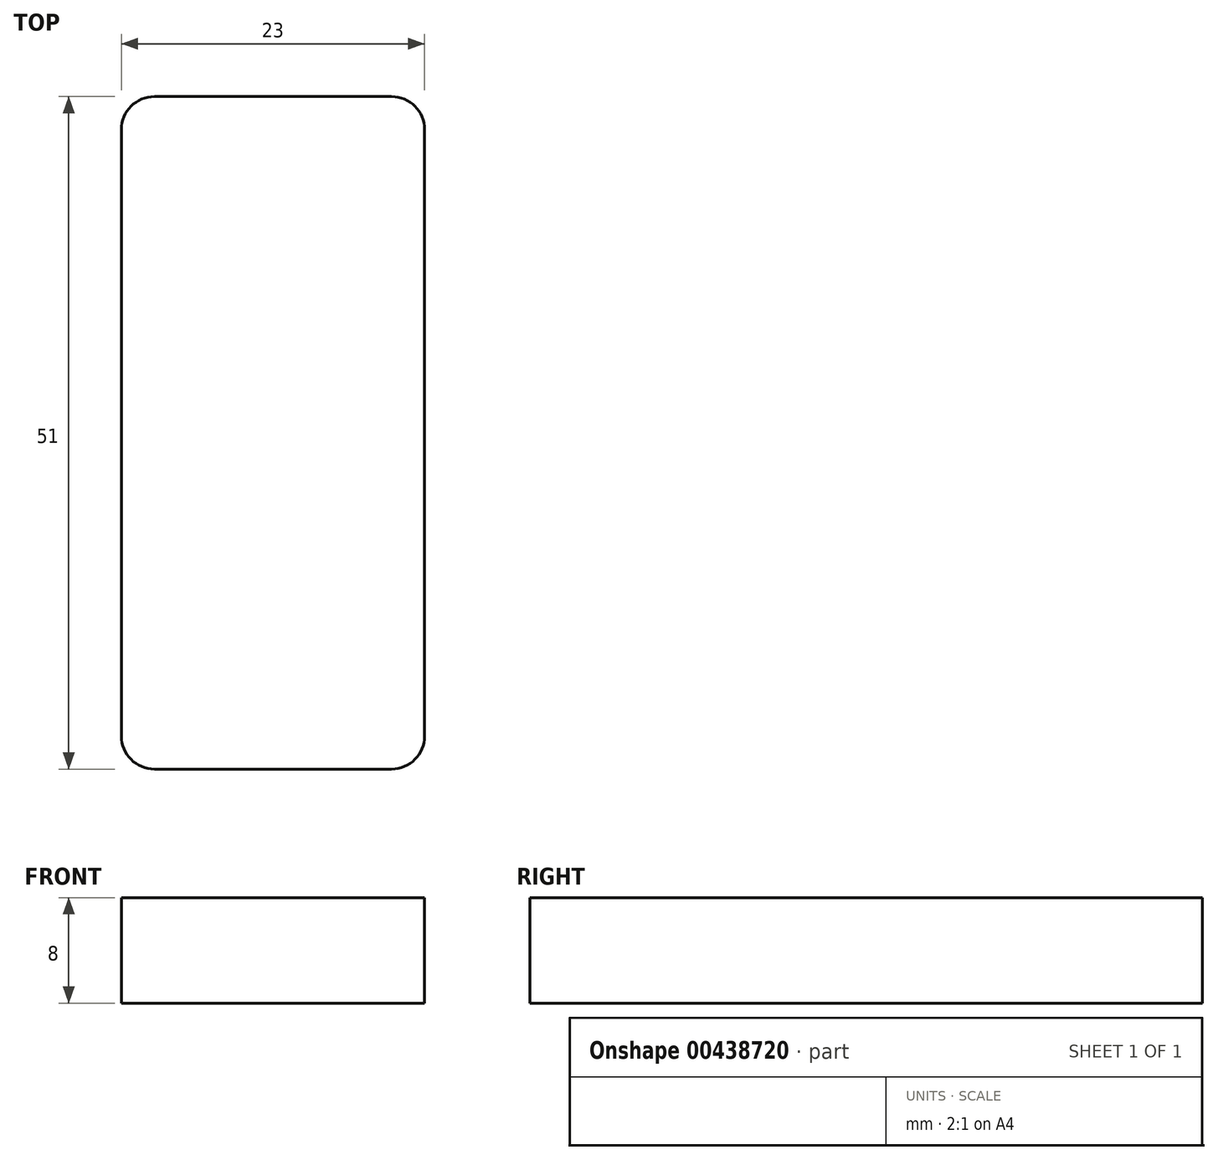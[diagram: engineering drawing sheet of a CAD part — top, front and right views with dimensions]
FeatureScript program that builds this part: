
annotation { "Feature Type Name" : "Feature", "Feature Type Description" : "" }
export const myFeature = defineFeature(function(context is Context, id is Id, definition is map)
    precondition{}
    {
        {
            var Q0;
            Q0=qCreatedBy(makeId("Top.planeOp"),FACE);
            var sketch = newSketch(context, id + "F0", { "sketchPlane" : qUnion([Q0])});
            skLineSegment(sketch, "E0.bottom", {"start": v(-11.5, -25.5) * mm, "end": v(11.5, -25.5) * mm});
            skLineSegment(sketch, "E0.top", {"start": v(-11.5, 25.5) * mm, "end": v(11.5, 25.5) * mm});
            skLineSegment(sketch, "E0.left", {"start": v(-11.5, -25.5) * mm, "end": v(-11.5, 25.5) * mm});
            skLineSegment(sketch, "E0.right", {"start": v(11.5, -25.5) * mm, "end": v(11.5, 25.5) * mm});
            skPoint(sketch, "E0.middle", {"position": v(0, 0) * mm});
            skSolve(sketch);
        }
        {
            var Q0;
            Q0=qSketchRegion(id+"F0",true);
            extrude(context, id + "F1", {"entities" : qUnion([Q0]), "depth" : 8 * mm});
        }
        {
            var Q0;
            Q0=makeQuery(id+"F1.opExtrude","SWEPT_EDGE",EDGE,{"disambiguationData":[OSD([sQuery(id+"F0.wireOp",EDGE,"E0.bottom"),sQuery(id+"F0.wireOp",EDGE,"E0.left")])]});
            var Q1;
            Q1=makeQuery(id+"F1.opExtrude","SWEPT_EDGE",EDGE,{"disambiguationData":[OSD([sQuery(id+"F0.wireOp",EDGE,"E0.bottom"),sQuery(id+"F0.wireOp",EDGE,"E0.right")])]});
            var Q2;
            Q2=makeQuery(id+"F1.opExtrude","SWEPT_EDGE",EDGE,{"disambiguationData":[OSD([sQuery(id+"F0.wireOp",EDGE,"E0.top"),sQuery(id+"F0.wireOp",EDGE,"E0.right")])]});
            var Q3;
            Q3=makeQuery(id+"F1.opExtrude","SWEPT_EDGE",EDGE,{"disambiguationData":[OSD([sQuery(id+"F0.wireOp",EDGE,"E0.top"),sQuery(id+"F0.wireOp",EDGE,"E0.left")])]});
            fillet(context, id + "F2", {"entities" : qUnion([Q0, Q1, Q2, Q3]), "radius" : 2.5 * mm, "tangentPropagation" : true, "allowEdgeOverflow" : false});
        }
        {
            var Q0;
            Q0=makeQuery(id+"F1.opExtrude","SWEPT_BODY",BODY,{"disambiguationData":[OSD([sQuery(id+"F0.wireOp",EDGE,"E0.bottom"),sQuery(id+"F0.wireOp",EDGE,"E0.top"),sQuery(id+"F0.wireOp",EDGE,"E0.left"),sQuery(id+"F0.wireOp",EDGE,"E0.right")])]});
            transform(context, id + "F3", {"entities" : qUnion([Q0]), "transformType" : TransformType.TRANSLATION_3D, "dx" : 0 * mm, "dy" : 0 * mm, "dz" : 0 * mm, "makeCopy" : true});
        }
    });
